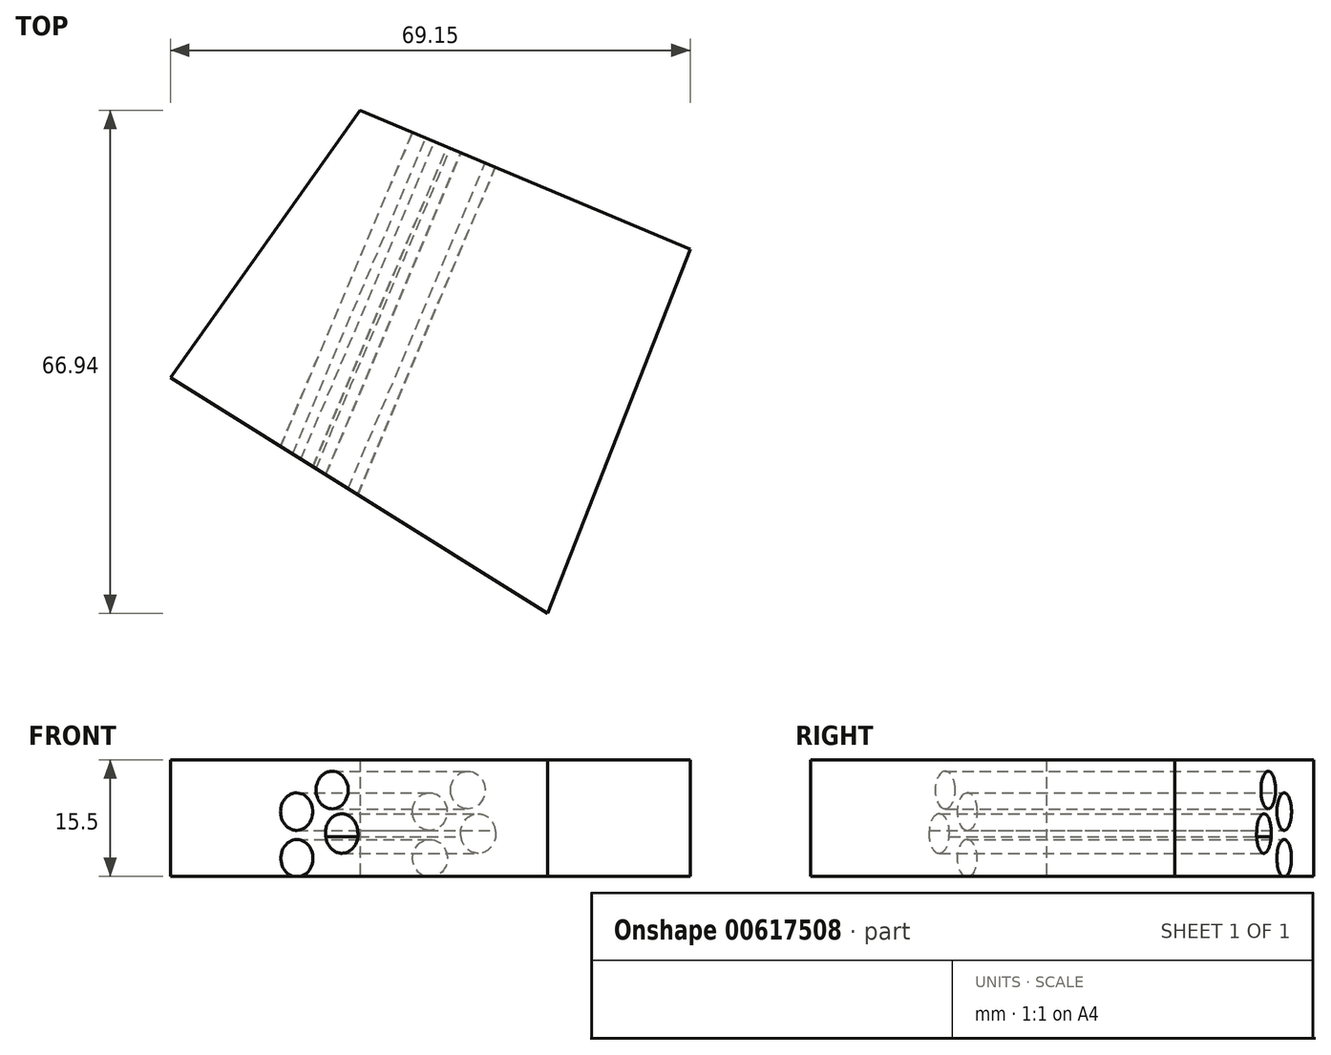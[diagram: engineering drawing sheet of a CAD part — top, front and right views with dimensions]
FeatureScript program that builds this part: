
annotation { "Feature Type Name" : "Feature", "Feature Type Description" : "" }
export const myFeature = defineFeature(function(context is Context, id is Id, definition is map)
    precondition{}
    {
        {
            var Q0;
            Q0=qCreatedBy(makeId("Top.planeOp"),FACE);
            var sketch = newSketch(context, id + "F0", { "sketchPlane" : qUnion([Q0])});
            skLineSegment(sketch, "E0", {"start": v(0, 35.56) * mm, "end": v(-25.22, 0) * mm});
            skLineSegment(sketch, "E1", {"start": v(-25.22, 0) * mm, "end": v(24.98, -31.38) * mm});
            skLineSegment(sketch, "E2", {"start": v(24.98, -31.38) * mm, "end": v(43.93, 17.1) * mm});
            skLineSegment(sketch, "E3", {"start": v(43.93, 17.1) * mm, "end": v(0, 35.56) * mm});
            skSolve(sketch);
        }
        {
            var Q0;
            Q0=makeQuery(id+"F0.imprint","IMPRINT",FACE,{"disambiguationData":[TD([[makeQuery(id+"F0.imprint","IMPRINT",EDGE,{"derivedFrom":sQuery(id+"F0.wireOp",EDGE,"E0")}),1.0]])]});
            extrude(context, id + "F1", {"entities" : qUnion([Q0]), "depth" : 15.5 * mm, "offsetDistance" : 25 * mm});
        }
        {
            var Q0;
            Q0=makeQuery(id+"F1.opExtrude","SWEPT_FACE",FACE,{"disambiguationData":[OSD([sQuery(id+"F0.wireOp",EDGE,"E3")])]});
            var sketch = newSketch(context, id + "F2", { "sketchPlane" : qUnion([Q0])});
            skLineSegment(sketch, "E4", {"start": v(3.7, 8.62) * mm, "end": v(-1.8, 11.5) * mm});
            skLineSegment(sketch, "E5", {"start": v(-1.8, 11.5) * mm, "end": v(-3.27, 5.83) * mm});
            skLineSegment(sketch, "E6", {"start": v(-3.3, 5.58) * mm, "end": v(3.66, 2.42) * mm});
            skLineSegment(sketch, "E7", {"start": v(3.66, 2.42) * mm, "end": v(3.7, 8.62) * mm});
            skSolve(sketch);
        }
        {
            var Q0;
            Q0=sQuery(id+"F2.wireOp",VERTEX,"E6.start");
            var Q1;
            Q1=sQuery(id+"F2.wireOp",VERTEX,"E4.start");
            var Q2;
            Q2=sQuery(id+"F2.wireOp",VERTEX,"E5.start");
            var Q3;
            Q3=sQuery(id+"F2.wireOp",VERTEX,"E7.start");
            var Q4;
            Q4=sQuery(id+"F2.wireOp",VERTEX,"E5.end");
            var Q5;
            Q5=makeQuery(id+"F1.opExtrude","SWEPT_BODY",BODY,{"disambiguationData":[OSD([sQuery(id+"F0.wireOp",EDGE,"E0"),sQuery(id+"F0.wireOp",EDGE,"E1"),sQuery(id+"F0.wireOp",EDGE,"E2"),sQuery(id+"F0.wireOp",EDGE,"E3")])]});
            hole(context, id + "F3", {"style" : HoleStyle.SIMPLE, "endStyle" : HoleEndStyle.THROUGH, "holeDiameter" : 5 * mm, "majorDiameter" : 5 * mm, "isTappedThrough" : true, "tappedDepth" : 12 * mm, "tapClearance" : 3, "locations" : qUnion([Q0, Q1, Q2, Q3, Q4]), "scope" : qUnion([Q5])});
        }
    });
